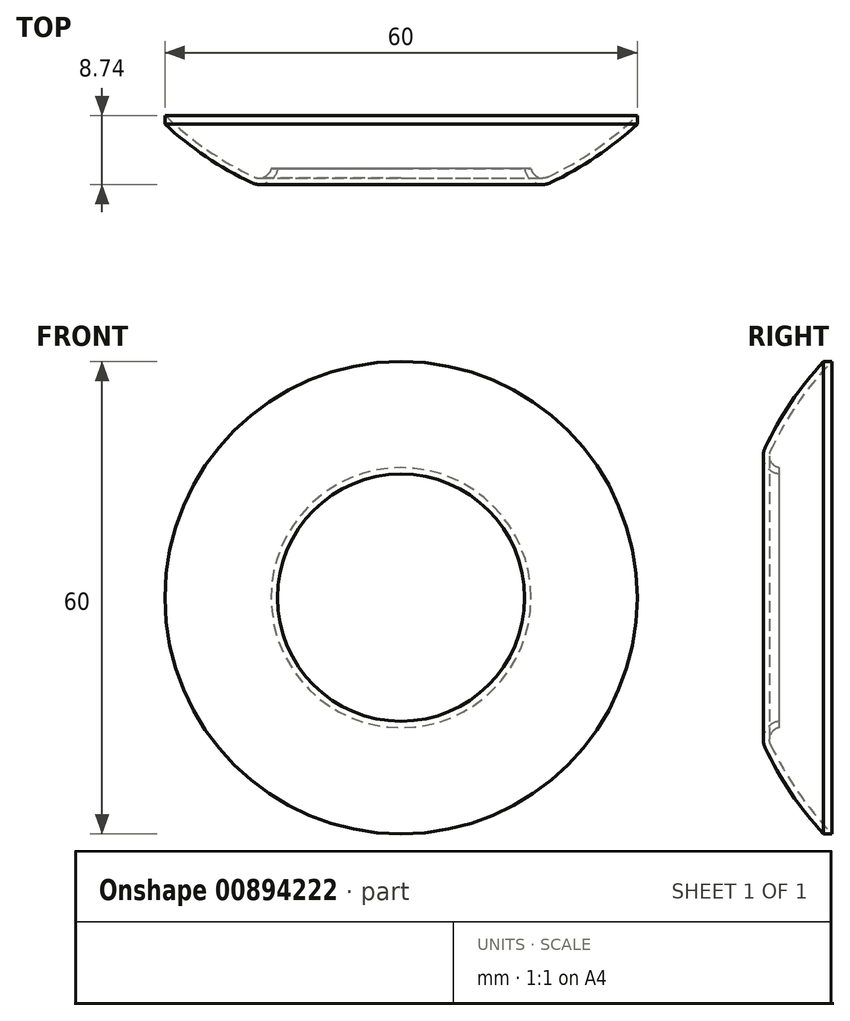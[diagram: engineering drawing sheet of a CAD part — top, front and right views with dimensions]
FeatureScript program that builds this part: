
annotation { "Feature Type Name" : "Feature", "Feature Type Description" : "" }
export const myFeature = defineFeature(function(context is Context, id is Id, definition is map)
    precondition{}
    {
        {
            var Q0;
            Q0=qCreatedBy(makeId("Right.planeOp"),FACE);
            var sketch = newSketch(context, id + "F0", { "sketchPlane" : qUnion([Q0])});
            skLineSegment(sketch, "E0", {"start": v(-31.5, 30) * mm, "end": v(-32.6, 30) * mm});
            skArc(sketch, "E1", {"start": v(-32.6, 30) * mm, "mid": v(-36.72, 24.78) * mm, "end": v(-40.02, 19) * mm});
            skLineSegment(sketch, "E2", {"start": v(0, 0) * mm, "end": v(-40.02, 0) * mm});
            skArc(sketch, "E3", {"start": v(-31.5, 30) * mm, "mid": v(-35.85, 24.64) * mm, "end": v(-39.3, 18.66) * mm});
            skArc(sketch, "E4", {"start": v(-40.02, 19) * mm, "mid": v(-39.97, 16.9) * mm, "end": v(-38.24, 15.7) * mm});
            skArc(sketch, "E5", {"start": v(-39.3, 18.66) * mm, "mid": v(-39.29, 17.33) * mm, "end": v(-38.24, 16.51) * mm});
            skLineSegment(sketch, "E6", {"start": v(-38.24, 15.7) * mm, "end": v(-38.24, 16.51) * mm});
            skSolve(sketch);
        }
        {
            var Q0;
            Q0=makeQuery(id+"F0.imprint","IMPRINT",FACE,{"disambiguationData":[TD([[makeQuery(id+"F0.imprint","IMPRINT",EDGE,{"derivedFrom":sQuery(id+"F0.wireOp",EDGE,"E0")}),1.0]])]});
            var Q1;
            Q1=sQuery(id+"F0.wireOp",EDGE,"E2");
            revolve(context, id + "F1", {"surfaceOperationType" : NewSurfaceOperationType.NEW, "entities" : qUnion([Q0]), "axis" : qUnion([Q1]), "revolveType" : RevolveType.FULL});
        }
    });
